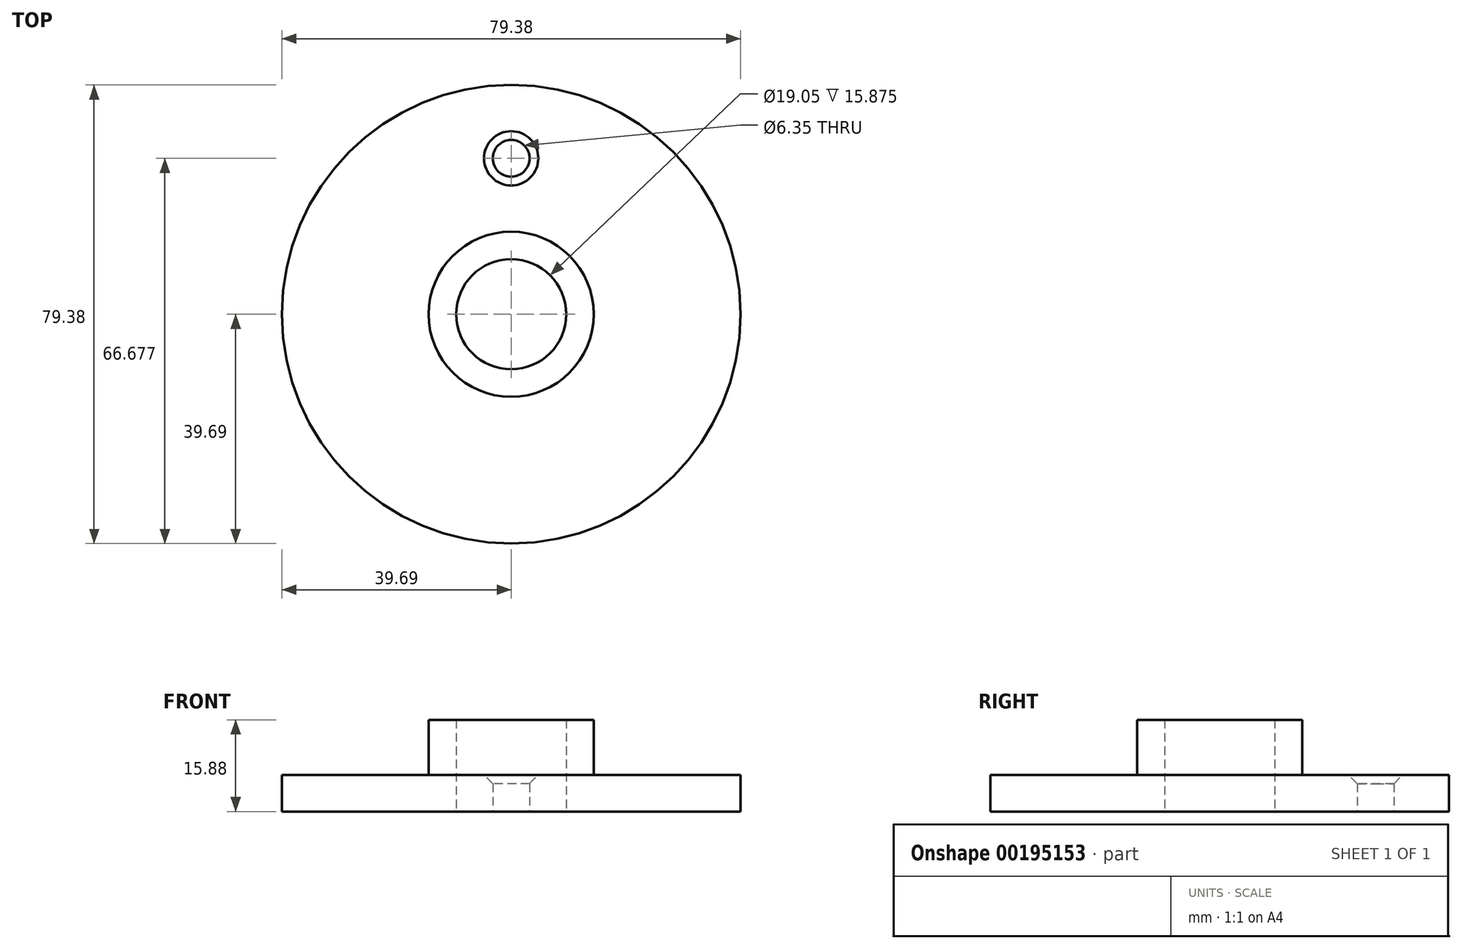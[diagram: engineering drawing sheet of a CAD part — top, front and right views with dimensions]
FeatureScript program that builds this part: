
annotation { "Feature Type Name" : "Feature", "Feature Type Description" : "" }
export const myFeature = defineFeature(function(context is Context, id is Id, definition is map)
    precondition{}
    {
        {
            var Q0;
            Q0=qCreatedBy(makeId("Front.planeOp"),FACE);
            var sketch = newSketch(context, id + "F0", { "sketchPlane" : qUnion([Q0])});
            skLineSegment(sketch, "E0", {"start": v(0, 0) * mm, "end": v(-39.69, 0) * mm});
            skLineSegment(sketch, "E1", {"start": v(-39.69, 0) * mm, "end": v(-39.69, 6.35) * mm});
            skLineSegment(sketch, "E2", {"start": v(-39.69, 6.35) * mm, "end": v(-14.29, 6.35) * mm});
            skLineSegment(sketch, "E3", {"start": v(-14.29, 6.35) * mm, "end": v(-14.29, 15.88) * mm});
            skLineSegment(sketch, "E4", {"start": v(-14.29, 15.88) * mm, "end": v(0, 15.88) * mm});
            skLineSegment(sketch, "E5", {"start": v(0, 0) * mm, "end": v(0, 45.35) * mm, "construction": true});
            skLineSegment(sketch, "E6", {"start": v(-9.53, 15.88) * mm, "end": v(-9.53, 0) * mm});
            skSolve(sketch);
        }
        {
            var Q0;
            {var subQ1=sQuery(id+"F0.wireOp",EDGE,"E1");Q0=makeQuery(id+"F0.imprint","IMPRINT",FACE,{"disambiguationData":[TD([[makeQuery(id+"F0.imprint","IMPRINT",EDGE,{"derivedFrom":subQ1}),-1.0]])]});}
            var Q1;
            Q1=sQuery(id+"F0.wireOp",EDGE,"E5");
            revolve(context, id + "F1", {"entities" : qUnion([Q0]), "axis" : qUnion([Q1]), "revolveType" : RevolveType.FULL});
        }
        {
            var Q0;
            Q0=qCreatedBy(makeId("Top.planeOp"),FACE);
            var sketch = newSketch(context, id + "F2", { "sketchPlane" : qUnion([Q0])});
            skCircle(sketch, "E7", {"center": v(0, 0) * mm, "radius": 26.99 * mm, "construction": true});
            skPoint(sketch, "E8", {"position": v(0, 26.99) * mm});
            skCircle(sketch, "E9", {"center": v(0, 26.99) * mm, "radius": 3.18 * mm});
            skSolve(sketch);
        }
        {
            var Q0;
            Q0=makeQuery(id+"F2.imprint","IMPRINT",FACE,{"disambiguationData":[TD([[makeQuery(id+"F2.imprint","IMPRINT",EDGE,{"derivedFrom":sQuery(id+"F2.wireOp",EDGE,"E9")}),1.0]])]});
            extrude(context, id + "F3", {"entities" : qUnion([Q0]), "operationType" : NewBodyOperationType.REMOVE, "endBound" : BoundingType.THROUGH_ALL, "depth" : 21.59 * mm});
        }
        {
            var Q0;
            Q0=makeQuery(id+"F3.boolean.opBoolean","INTERSECT",EDGE,{"derivedFrom":[makeQuery(id+"F1.opRevolve","SWEPT_FACE",FACE,{"disambiguationData":[OSD([sQuery(id+"F0.wireOp",EDGE,"E2")])]}),makeQuery(id+"F3.opExtrude","SWEPT_FACE",FACE,{"disambiguationData":[OSD([sQuery(id+"F2.wireOp",EDGE,"E9")])]})]});
            chamfer(context, id + "F4", {"entities" : qUnion([Q0]), "width" : 1.52 * mm, "tangentPropagation" : true});
        }
    });
